# Revit family: Hager-Univers-IP44-syst-Surface_mounted-PL-en
name_source: partatom
category: Electrical Equipment
units: mm (PartAtom-declared; Revit-internal decimal feet)

## family parameters
Cut with Voids When Loaded = No
Host = Face
Panel Configuration = Two Columns, Circuits Across
Part Type = Panelboard
Room Calculation Point = No
Round Connector Dimension = Use Diameter
Shared = No

## types (33) — shared parameters
EF000007 - Colour = EV000202 - White
EF000049 - Depth = 161 mm  [stored 0.528215 ft]
EF000116 - RAL-number = 9010
EF000118 - With mounting plate = No
EF000339 - Type of cover = EV004216 - Door
EF001062 - EMC-version = No
EF001088 - Extension possible = Yes
EF001134 - DIN-rail = Yes
EF001596 - Material housing = EV000179 - Steel
EF004462 - Type of closure = EV000154 - Other
EF005474 - Degree of protection (IP) = EV006418 - IP44
EF006244 - Transparent cover/door = No
EF006306 - With lock = No
EF015941 - Signal passing door = No
HG000002 - With door or cover = Yes
HG000003 - Range = Univers
HG000005 - Thickness = 3 mm  [stored 0.00984252 ft]
HG000006 - Flush mounted = No
HG000011 - Empty rows from bottom = No
HG000017 - Distance between poles = 18 mm  [stored 0.0590551 ft]
Manufacturer = Hager
Type Comments = Univers
zero-valued in all types: Default Elevation, HG000007 - Number of empty columns

## per-type parameters (varying)
| type | EF000003 - Mounting method | EF000008 - Width | EF000040 - Height | EF000218 - Built-in depth | EF000266 - Number of rows | EF000332 - Built-in height | EF000846 - Built-in width | EF001131 - Internal depth | EF002950 - Width in number of modular spacings | EF009212 - Cover model | EF015776 - Earthing terminal block | EF015777 - Neutral terminal block | HG000001 - Number of columns | HG000004 - Manufacturer reference | HG000008 - Number of empty rows | HG000009 - Double swing door | HG000010 - Asymmetric doors | Model |
| Surface mounted IP44 W1050 H1100 D161 12 Modular spacings - FWB74N | EV001247 - Surface mounted/recessed mounted | 1050 mm | 1100 mm | 161 mm  [stored 0.528215 ft] | 20 | 1100 mm | 1050 mm | 161 mm  [stored 0.528215 ft] | 12 | EV009916 - With notch | No | No | 4 | FWB74N | 8 | Yes | No | FWB74N |
| Surface mounted IP44 W1050 H1100 D161 12 Modular spacings - FWB74S | EV001247 - Surface mounted/recessed mounted | 1050 mm | 1100 mm | 161 mm  [stored 0.528215 ft] | 28 | 1100 mm | 1050 mm | 161 mm  [stored 0.528215 ft] | 12 | EV009916 - With notch | No | No | 4 | FWB74S | 0 | Yes | No | FWB74S |
| Surface mounted IP44 W1050 H500 D161 12 Modular spacings - FWB34S | EV001247 - Surface mounted/recessed mounted | 1050 mm | 500 mm  [stored 1.64042 ft] | 161 mm  [stored 0.528215 ft] | 12 | 500 mm  [stored 1.64042 ft] | 1050 mm | 161 mm  [stored 0.528215 ft] | 12 | EV009916 - With notch | Yes | Yes | 4 | FWB34S | 0 | Yes | No | FWB34S |
| Surface mounted IP44 W1050 H650 D161 12 Modular spacings - FWB44S | EV001247 - Surface mounted/recessed mounted | 1050 mm | 650 mm  [stored 2.13255 ft] | 161 mm  [stored 0.528215 ft] | 16 | 650 mm  [stored 2.13255 ft] | 1050 mm | 161 mm  [stored 0.528215 ft] | 12 | EV009916 - With notch | Yes | Yes | 4 | FWB44S | 0 | Yes | No | FWB44S |
| Surface mounted IP44 W1050 H800 D161 12 Modular spacings - FWB54S | EV001247 - Surface mounted/recessed mounted | 1050 mm | 800 mm  [stored 2.62467 ft] | 161 mm  [stored 0.528215 ft] | 20 | 800 mm  [stored 2.62467 ft] | 1050 mm | 161 mm  [stored 0.528215 ft] | 12 | EV009916 - With notch | Yes | Yes | 4 | FWB54S | 0 | Yes | No | FWB54S |
| Surface mounted IP44 W1050 H950 D161 12 Modular spacings - FWB64N | EV001247 - Surface mounted/recessed mounted | 1050 mm | 950 mm  [stored 3.1168 ft] | 161 mm  [stored 0.528215 ft] | 16 | 950 mm  [stored 3.1168 ft] | 1050 mm | 161 mm  [stored 0.528215 ft] | 12 | EV009916 - With notch | No | No | 4 | FWB64N | 8 | Yes | No | FWB64N |
| Surface mounted IP44 W1050 H950 D161 12 Modular spacings - FWB64S | EV001247 - Surface mounted/recessed mounted | 1050 mm | 950 mm  [stored 3.1168 ft] | 161 mm  [stored 0.528215 ft] | 24 | 950 mm  [stored 3.1168 ft] | 1050 mm | 161 mm  [stored 0.528215 ft] | 12 | EV009916 - With notch | Yes | Yes | 4 | FWB64S | 0 | Yes | No | FWB64S |
| Surface mounted IP44 W300 H1100 D161 12 Modular spacings - FWB71S | EV001247 - Surface mounted/recessed mounted | 300 mm | 1100 mm | 161 mm  [stored 0.528215 ft] | 7 | 1100 mm | 300 mm | 161 mm  [stored 0.528215 ft] | 12 | EV009916 - With notch | Yes | Yes | 1 | FWB71S | 0 | No | No | FWB71S |
| Surface mounted IP44 W300 H500 D161 12 Modular spacings - FWB31S | EV001247 - Surface mounted/recessed mounted | 300 mm | 500 mm  [stored 1.64042 ft] | 161 mm  [stored 0.528215 ft] | 3 | 500 mm  [stored 1.64042 ft] | 300 mm | 161 mm  [stored 0.528215 ft] | 12 | EV009916 - With notch | Yes | Yes | 1 | FWB31S | 0 | No | No | FWB31S |
| Surface mounted IP44 W300 H650 D161 12 Modular spacings - FWB41S | EV001247 - Surface mounted/recessed mounted | 300 mm | 650 mm  [stored 2.13255 ft] | 161 mm  [stored 0.528215 ft] | 4 | 650 mm  [stored 2.13255 ft] | 300 mm | 160 mm  [stored 0.524934 ft] | 12 | EV009916 - With notch | Yes | Yes | 1 | FWB41S | 0 | No | No | FWB41S |
| Surface mounted IP44 W300 H800 D161 12 Modular spacings - FWB51S | EV001247 - Surface mounted/recessed mounted | 300 mm | 800 mm  [stored 2.62467 ft] | 161 mm  [stored 0.528215 ft] | 5 | 800 mm  [stored 2.62467 ft] | 300 mm | 161 mm  [stored 0.528215 ft] | 12 | EV009916 - With notch | Yes | Yes | 1 | FWB51S | 0 | No | No | FWB51S |
| Surface mounted IP44 W300 H950 D161 12 Modular spacings - FWB61S | EV001247 - Surface mounted/recessed mounted | 300 mm | 950 mm  [stored 3.1168 ft] | 161 mm  [stored 0.528215 ft] | 6 | 950 mm  [stored 3.1168 ft] | 300 mm | 161 mm  [stored 0.528215 ft] | 12 | EV009916 - With notch | Yes | Yes | 1 | FWB61S | 0 | No | No | FWB61S |
| Surface mounted IP44 W550 H1100 D161 12 Modular spacings - FWB72N | EV001247 - Surface mounted/recessed mounted | 550 mm | 1100 mm | 161 mm  [stored 0.528215 ft] | 10 | 1100 mm | 550 mm | 161 mm  [stored 0.528215 ft] | 12 | EV009916 - With notch | No | No | 2 | FWB72N | 4 | No | No | FWB72N |
| Surface mounted IP44 W550 H1100 D161 12 Modular spacings - FWB72S | EV001247 - Surface mounted/recessed mounted | 550 mm | 1100 mm | 161 mm  [stored 0.528215 ft] | 14 | 1100 mm | 550 mm | 161 mm  [stored 0.528215 ft] | 12 | EV009916 - With notch | No | No | 2 | FWB72S | 0 | No | No | FWB72S |
| Surface mounted IP44 W550 H1100 D161 26 Modular spacings - FWB72M2 | EV000384 - Surface mounted (plaster) | 550 mm | 1100 mm | 0 mm  [stored 0 ft] | 7 | 0 mm  [stored 0 ft] | 0 mm  [stored 0 ft] | 161 mm  [stored 0.528215 ft] | 26 | EV000116 - Closed | No | No | 1 | FWB72M2 | 0 | No | No | FWB72M2 |
| Surface mounted IP44 W550 H500 D161 12 Modular spacings - FWB32S | EV001247 - Surface mounted/recessed mounted | 550 mm | 500 mm  [stored 1.64042 ft] | 161 mm  [stored 0.528215 ft] | 6 | 500 mm  [stored 1.64042 ft] | 550 mm | 161 mm  [stored 0.528215 ft] | 12 | EV009916 - With notch | Yes | Yes | 2 | FWB32S | 0 | No | No | FWB32S |
| Surface mounted IP44 W550 H500 D161 26 Modular spacings - FWB32M2 | EV000384 - Surface mounted (plaster) | 550 mm | 500 mm  [stored 1.64042 ft] | 0 mm  [stored 0 ft] | 3 | 0 mm  [stored 0 ft] | 0 mm  [stored 0 ft] | 161 mm  [stored 0.528215 ft] | 26 | EV000116 - Closed | No | No | 1 | FWB32M2 | 0 | No | No | FWB32M2 |
| Surface mounted IP44 W550 H650 D161 12 Modular spacings - FWB42S | EV001247 - Surface mounted/recessed mounted | 550 mm | 650 mm  [stored 2.13255 ft] | 161 mm  [stored 0.528215 ft] | 8 | 650 mm  [stored 2.13255 ft] | 550 mm | 161 mm  [stored 0.528215 ft] | 12 | EV009916 - With notch | No | No | 2 | FWB42S | 0 | No | No | FWB42S |
| Surface mounted IP44 W550 H650 D161 26 Modular spacings - FWB42M2 | EV000384 - Surface mounted (plaster) | 550 mm | 650 mm  [stored 2.13255 ft] | 0 mm  [stored 0 ft] | 4 | 0 mm  [stored 0 ft] | 0 mm  [stored 0 ft] | 161 mm  [stored 0.528215 ft] | 26 | EV000116 - Closed | No | No | 1 | FWB42M2 | 0 | No | No | FWB42M2 |
| Surface mounted IP44 W550 H800 D161 12 Modular spacings - FWB52N | EV001247 - Surface mounted/recessed mounted | 550 mm | 800 mm  [stored 2.62467 ft] | 161 mm  [stored 0.528215 ft] | 6 | 800 mm  [stored 2.62467 ft] | 550 mm | 161 mm  [stored 0.528215 ft] | 12 | EV009916 - With notch | No | No | 2 | FWB52N | 4 | No | No | FWB52N |
| Surface mounted IP44 W550 H800 D161 12 Modular spacings - FWB52S | EV001247 - Surface mounted/recessed mounted | 550 mm | 800 mm  [stored 2.62467 ft] | 161 mm  [stored 0.528215 ft] | 10 | 800 mm  [stored 2.62467 ft] | 550 mm | 161 mm  [stored 0.528215 ft] | 12 |  | Yes | Yes | 2 | FWB52S | 0 | No | No | FWB52S |
| Surface mounted IP44 W550 H800 D161 26 Modular spacings - FWB52M2 | EV000384 - Surface mounted (plaster) | 550 mm | 800 mm  [stored 2.62467 ft] | 0 mm  [stored 0 ft] | 5 | 0 mm  [stored 0 ft] | 0 mm  [stored 0 ft] | 161 mm  [stored 0.528215 ft] | 26 | EV000116 - Closed | No | No | 1 | FWB52M2 | 0 | No | No | FWB52M2 |
| Surface mounted IP44 W550 H950 D161 12 Modular spacings - FWB62N | EV001247 - Surface mounted/recessed mounted | 550 mm | 950 mm  [stored 3.1168 ft] | 161 mm  [stored 0.528215 ft] | 8 | 950 mm  [stored 3.1168 ft] | 550 mm | 161 mm  [stored 0.528215 ft] | 12 | EV009916 - With notch | No | No | 2 | FWB62N | 4 | No | No | FWB62N |
| Surface mounted IP44 W550 H950 D161 12 Modular spacings - FWB62S | EV001247 - Surface mounted/recessed mounted | 550 mm | 950 mm  [stored 3.1168 ft] | 161 mm  [stored 0.528215 ft] | 12 | 950 mm  [stored 3.1168 ft] | 550 mm | 160 mm  [stored 0.524934 ft] | 12 | EV009916 - With notch | Yes | Yes | 2 | FWB62S | 0 | No | No | FWB62S |
| Surface mounted IP44 W550 H950 D161 26 Modular spacings - FWB62M2 | EV000384 - Surface mounted (plaster) | 550 mm | 950 mm  [stored 3.1168 ft] | 0 mm  [stored 0 ft] | 6 | 0 mm  [stored 0 ft] | 0 mm  [stored 0 ft] | 161 mm  [stored 0.528215 ft] | 26 | EV000116 - Closed | No | No | 1 | FWB62M2 | 0 | No | No | FWB62M2 |
| Surface mounted IP44 W800 H1100 D161 12 Modular spacings - FWB73N | EV001247 - Surface mounted/recessed mounted | 800 mm  [stored 2.62467 ft] | 1100 mm | 161 mm  [stored 0.528215 ft] | 15 | 1100 mm | 800 mm  [stored 2.62467 ft] | 161 mm  [stored 0.528215 ft] | 12 | EV009916 - With notch | No | No | 3 | FWB73N | 6 | Yes | Yes | FWB73N |
| Surface mounted IP44 W800 H1100 D161 12 Modular spacings - FWB73S | EV001247 - Surface mounted/recessed mounted | 800 mm  [stored 2.62467 ft] | 1100 mm | 161 mm  [stored 0.528215 ft] | 21 | 1100 mm | 800 mm  [stored 2.62467 ft] | 161 mm  [stored 0.528215 ft] | 12 | EV009916 - With notch | No | No | 3 | FWB73S | 0 | Yes | Yes | FWB73S |
| Surface mounted IP44 W800 H500 D161 12 Modular spacings - FWB33S | EV001247 - Surface mounted/recessed mounted | 800 mm  [stored 2.62467 ft] | 500 mm  [stored 1.64042 ft] | 161 mm  [stored 0.528215 ft] | 9 | 500 mm  [stored 1.64042 ft] | 800 mm  [stored 2.62467 ft] | 161 mm  [stored 0.528215 ft] | 12 | EV009916 - With notch | Yes | Yes | 3 | FWB33S | 0 | Yes | Yes | FWB33S |
| Surface mounted IP44 W800 H650 D161 12 Modular spacings - FWB43S | EV001247 - Surface mounted/recessed mounted | 800 mm  [stored 2.62467 ft] | 650 mm  [stored 2.13255 ft] | 161 mm  [stored 0.528215 ft] | 12 | 650 mm  [stored 2.13255 ft] | 800 mm  [stored 2.62467 ft] | 160 mm  [stored 0.524934 ft] | 12 | EV009916 - With notch | Yes | Yes | 3 | FWB43S | 0 | Yes | Yes | FWB43S |
| Surface mounted IP44 W800 H800 D161 12 Modular spacings - FWB53N | EV001247 - Surface mounted/recessed mounted | 800 mm  [stored 2.62467 ft] | 800 mm  [stored 2.62467 ft] | 161 mm  [stored 0.528215 ft] | 9 | 800 mm  [stored 2.62467 ft] | 800 mm  [stored 2.62467 ft] | 161 mm  [stored 0.528215 ft] | 12 | EV009916 - With notch | No | No | 3 | FWB53N | 6 | Yes | Yes | FWB53N |
| Surface mounted IP44 W800 H800 D161 12 Modular spacings - FWB53S | EV001247 - Surface mounted/recessed mounted | 800 mm  [stored 2.62467 ft] | 800 mm  [stored 2.62467 ft] | 161 mm  [stored 0.528215 ft] | 15 | 800 mm  [stored 2.62467 ft] | 800 mm  [stored 2.62467 ft] | 160 mm  [stored 0.524934 ft] | 12 | EV009916 - With notch | Yes | Yes | 3 | FWB53S | 0 | Yes | Yes | FWB53S |
| Surface mounted IP44 W800 H950 D161 12 Modular spacings - FWB63N | EV001247 - Surface mounted/recessed mounted | 800 mm  [stored 2.62467 ft] | 950 mm  [stored 3.1168 ft] | 161 mm  [stored 0.528215 ft] | 12 | 950 mm  [stored 3.1168 ft] | 800 mm  [stored 2.62467 ft] | 161 mm  [stored 0.528215 ft] | 12 | EV009916 - With notch | No | No | 3 | FWB63N | 6 | Yes | Yes | FWB63N |
| Surface mounted IP44 W800 H950 D161 12 Modular spacings - FWB63S | EV001247 - Surface mounted/recessed mounted | 800 mm  [stored 2.62467 ft] | 950 mm  [stored 3.1168 ft] | 161 mm  [stored 0.528215 ft] | 18 | 950 mm  [stored 3.1168 ft] | 800 mm  [stored 2.62467 ft] | 160 mm  [stored 0.524934 ft] | 12 | EV009916 - With notch | Yes | Yes | 3 | FWB63S | 0 | Yes | Yes | FWB63S |

note: [stored X ft] marks values corroborated as IEEE doubles in the binary element streams (Revit-internal decimal feet)

## geometry (parser evidence)
native form markers: Sweep x17
no freeform markers — native parametric forms only
